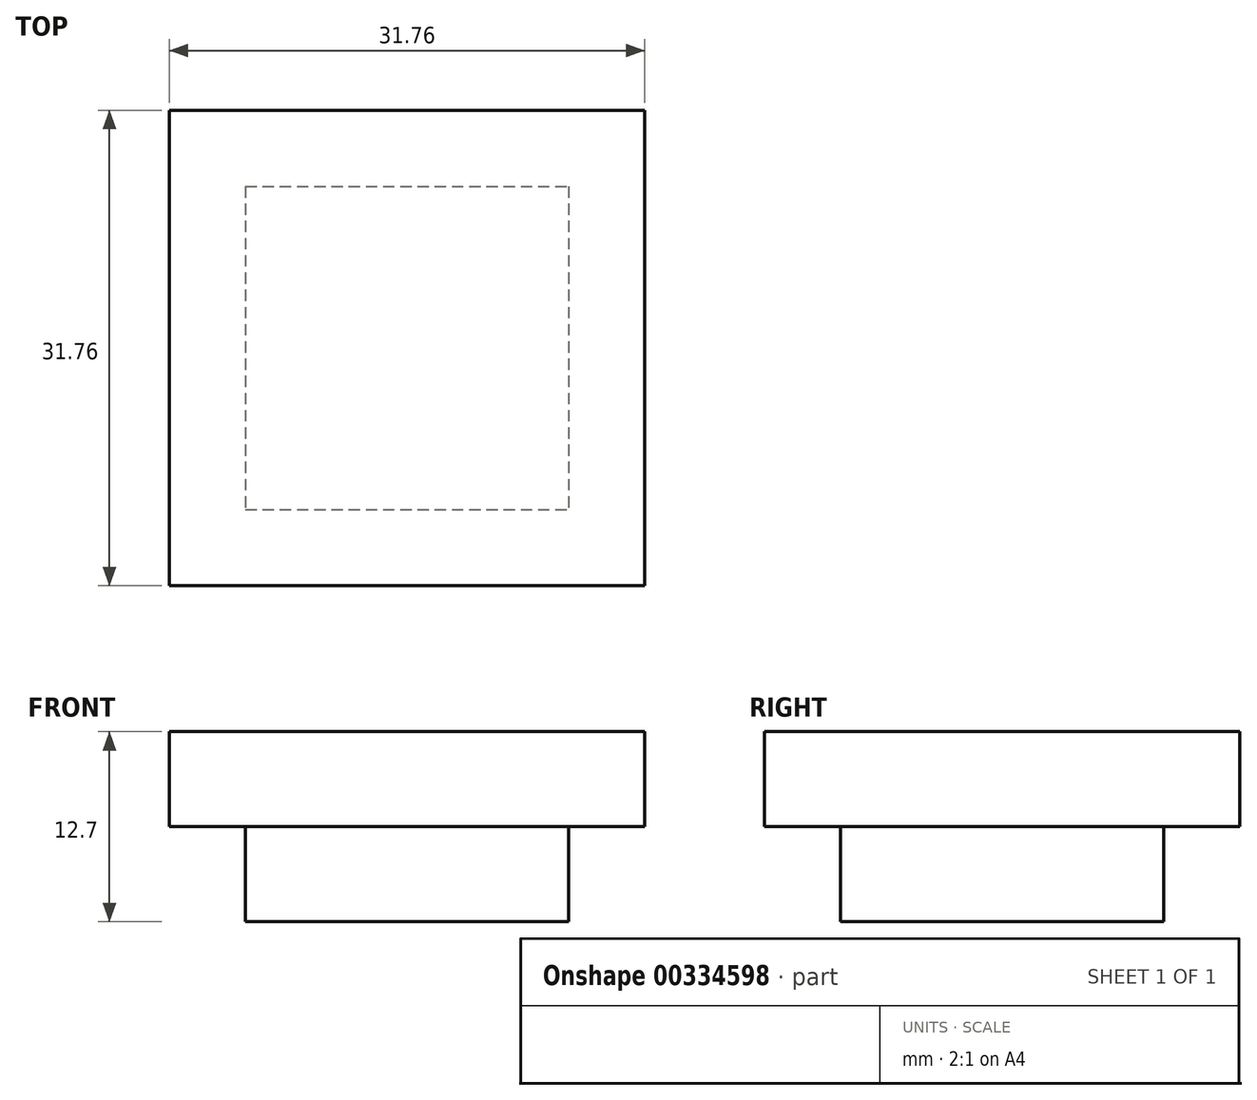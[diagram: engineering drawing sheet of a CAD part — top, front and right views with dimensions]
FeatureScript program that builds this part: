
annotation { "Feature Type Name" : "Feature", "Feature Type Description" : "" }
export const myFeature = defineFeature(function(context is Context, id is Id, definition is map)
    precondition{}
    {
        {
            var Q0;
            Q0=qCreatedBy(makeId("Top.planeOp"),FACE);
            var sketch = newSketch(context, id + "F0", { "sketchPlane" : qUnion([Q0])});
            skLineSegment(sketch, "E0.bottom", {"start": v(-10.8, 10.8) * mm, "end": v(10.8, 10.8) * mm});
            skLineSegment(sketch, "E0.top", {"start": v(-10.8, -10.8) * mm, "end": v(10.8, -10.8) * mm});
            skLineSegment(sketch, "E0.left", {"start": v(-10.8, 10.8) * mm, "end": v(-10.8, -10.8) * mm});
            skLineSegment(sketch, "E0.right", {"start": v(10.8, 10.8) * mm, "end": v(10.8, -10.8) * mm});
            skPoint(sketch, "E0.middle", {"position": v(0, 0) * mm});
            skSolve(sketch);
        }
        {
            var Q0;
            Q0=makeQuery(id+"F0.imprint","IMPRINT",FACE,{"disambiguationData":[TD([[makeQuery(id+"F0.imprint","IMPRINT",EDGE,{"derivedFrom":sQuery(id+"F0.wireOp",EDGE,"E0.bottom")}),-1.0]])]});
            extrude(context, id + "F1", {"entities" : qUnion([Q0]), "depth" : 6.35 * mm});
        }
        {
            var Q0;
            Q0=makeQuery(id+"F1.opExtrude","CAP_FACE",FACE,{"disambiguationData":[OSD([sQuery(id+"F0.wireOp",EDGE,"E0.bottom"),sQuery(id+"F0.wireOp",EDGE,"E0.top"),sQuery(id+"F0.wireOp",EDGE,"E0.left"),sQuery(id+"F0.wireOp",EDGE,"E0.right")])],"isStart":false});
            var sketch = newSketch(context, id + "F2", { "sketchPlane" : qUnion([Q0])});
            skLineSegment(sketch, "E1.bottom", {"start": v(-15.87, 15.88) * mm, "end": v(15.88, 15.88) * mm});
            skLineSegment(sketch, "E1.top", {"start": v(-15.88, -15.88) * mm, "end": v(15.87, -15.88) * mm});
            skLineSegment(sketch, "E1.left", {"start": v(-15.87, 15.88) * mm, "end": v(-15.88, -15.87) * mm});
            skLineSegment(sketch, "E1.right", {"start": v(15.88, 15.88) * mm, "end": v(15.87, -15.87) * mm});
            skPoint(sketch, "E1.middle", {"position": v(0, 0) * mm});
            skSolve(sketch);
        }
        {
            var Q0;
            Q0=qSketchRegion(id+"F2",true);
            extrude(context, id + "F3", {"entities" : qUnion([Q0]), "operationType" : NewBodyOperationType.ADD, "depth" : 6.35 * mm});
        }
    });
